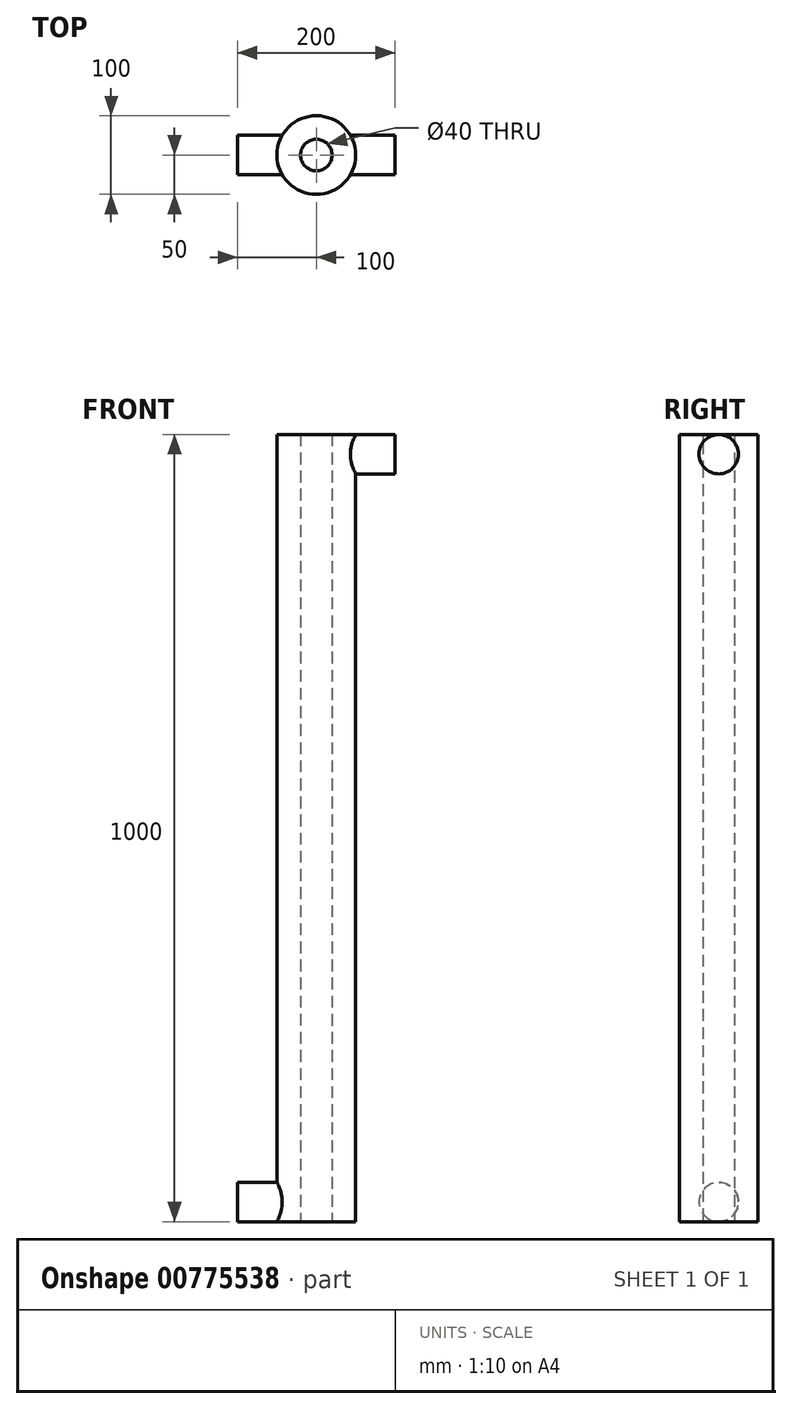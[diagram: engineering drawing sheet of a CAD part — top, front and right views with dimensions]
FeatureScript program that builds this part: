
annotation { "Feature Type Name" : "Feature", "Feature Type Description" : "" }
export const myFeature = defineFeature(function(context is Context, id is Id, definition is map)
    precondition{}
    {
        {
            var Q0;
            Q0=qCreatedBy(makeId("Top.planeOp"),FACE);
            var sketch = newSketch(context, id + "F0", { "sketchPlane" : qUnion([Q0])});
            skCircle(sketch, "E0", {"center": v(0, 0) * mm, "radius": 20 * mm});
            skCircle(sketch, "E1", {"center": v(0, 0) * mm, "radius": 50 * mm});
            skSolve(sketch);
        }
        {
            var Q0;
            Q0 = qSketchRegion(id + "F0", true);
            extrude(context, id + "F1", {"entities" : qUnion([Q0]), "endBound" : BoundingType.SYMMETRIC, "depth" : 1000 * mm, "offsetDistance" : 25.4 * mm});
        }
        {
            var Q0;
            Q0=qCreatedBy(makeId("Right.planeOp"),FACE);
            var sketch = newSketch(context, id + "F2", { "sketchPlane" : qUnion([Q0])});
            skCircle(sketch, "E2", {"center": v(0, 475) * mm, "radius": 25 * mm});
            skSolve(sketch);
        }
        {
            var Q0;
            Q0 = qSketchRegion(id + "F2", true);
            var Q1;
            Q1=makeQuery(id+"F1.opExtrude","SWEPT_FACE",FACE,{"disambiguationData":[OSD([sQuery(id+"F0.wireOp",EDGE,"E1")])]});
            extrude(context, id + "F3", {"entities" : qUnion([Q0]), "operationType" : NewBodyOperationType.ADD, "depth" : 100 * mm, "offsetDistance" : 25 * mm, "hasSecondDirection" : true, "secondDirectionBound" : SecondDirectionBoundingType.UP_TO_SURFACE, "secondDirectionOppositeDirection" : false, "secondDirectionDepth" : 25 * mm, "secondDirectionBoundEntityFace" : qUnion([Q1]), "hasSecondDirectionOffset" : true, "secondDirectionOffsetDistance" : 0 * mm});
        }
        {
            var Q0;
            Q0=qCreatedBy(makeId("Right.planeOp"),FACE);
            var sketch = newSketch(context, id + "F4", { "sketchPlane" : qUnion([Q0])});
            skCircle(sketch, "E3", {"center": v(0, -475) * mm, "radius": 25 * mm});
            skSolve(sketch);
        }
        {
            var Q0;
            Q0 = qSketchRegion(id + "F4", true);
            var Q1;
            Q1=makeQuery(id+"F1.opExtrude","SWEPT_FACE",FACE,{"disambiguationData":[OSD([sQuery(id+"F0.wireOp",EDGE,"E1")])]});
            extrude(context, id + "F5", {"entities" : qUnion([Q0]), "operationType" : NewBodyOperationType.ADD, "oppositeDirection" : true, "depth" : 100 * mm, "offsetDistance" : 25 * mm, "hasSecondDirection" : true, "secondDirectionBound" : SecondDirectionBoundingType.UP_TO_SURFACE, "secondDirectionOppositeDirection" : true, "secondDirectionDepth" : 25 * mm, "secondDirectionBoundEntityFace" : qUnion([Q1]), "hasSecondDirectionOffset" : true, "secondDirectionOffsetDistance" : 0 * mm});
        }
    });
